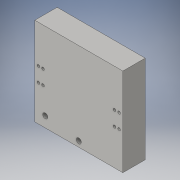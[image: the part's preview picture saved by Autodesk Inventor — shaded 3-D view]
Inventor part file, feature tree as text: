
AUTODESK INVENTOR PART (.ipt)
format: ipt  version: 2016 (Build 200138000, 138)  size: 106,496 bytes
history: native  units: in
note: dims shown in document units (in); Inventor stores cm internally (conversion verified against a paired STEP export)
features: extrude x1, sketch x1
ambient origin geometry x8: Origin, YZ Plane, XZ Plane, XY Plane, X Axis, Y Axis, Z Axis, Center Point
bodies: Body1 (feature_tree)
feature tree (2):
  extrude  "Extrusion3"  Depth=3.937in
  sketch  "Sketch1"  dims[d0=3.937in d1=3.937in d2=0.225in d8=0.225in d19=0.119in d24=0.085in d25=0.524in d26=1.0in d27=0.0in]
